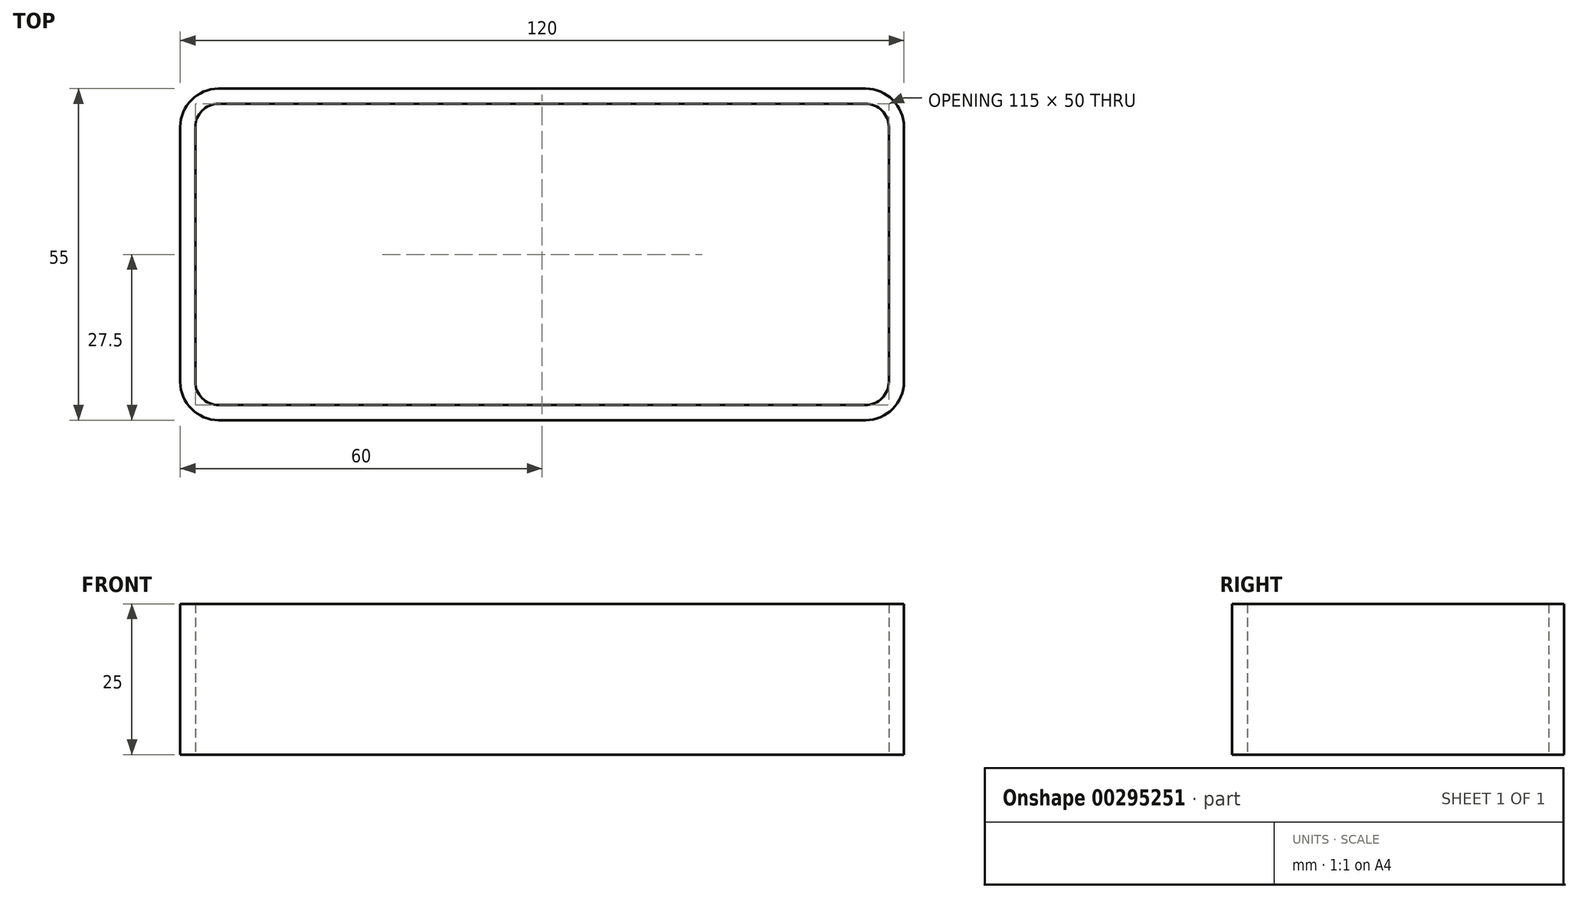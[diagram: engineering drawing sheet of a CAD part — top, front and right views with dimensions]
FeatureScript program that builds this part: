
annotation { "Feature Type Name" : "Feature", "Feature Type Description" : "" }
export const myFeature = defineFeature(function(context is Context, id is Id, definition is map)
    precondition{}
    {
        {
            var Q0;
            Q0=qCreatedBy(makeId("Top.planeOp"),FACE);
            var sketch = newSketch(context, id + "F0", { "sketchPlane" : qUnion([Q0])});
            skLineSegment(sketch, "E0.bottom", {"start": v(53.65, 27.5) * mm, "end": v(-53.65, 27.5) * mm});
            skLineSegment(sketch, "E0.top", {"start": v(53.65, -27.5) * mm, "end": v(-53.65, -27.5) * mm});
            skLineSegment(sketch, "E0.left", {"start": v(60, 21.15) * mm, "end": v(60, -21.15) * mm});
            skLineSegment(sketch, "E0.right", {"start": v(-60, 21.15) * mm, "end": v(-60, -21.15) * mm});
            skPoint(sketch, "E0.middle", {"position": v(0, 0) * mm});
            skPoint(sketch, "E1.visualSharp", {"position": v(-60, 27.5) * mm});
            skArc(sketch, "E1.filletArc", {"start": v(-53.65, 27.5) * mm, "mid": v(-58.14, 25.64) * mm, "end": v(-60, 21.15) * mm});
            skPoint(sketch, "E2.visualSharp", {"position": v(-60, -27.5) * mm});
            skArc(sketch, "E2.filletArc", {"start": v(-60, -21.15) * mm, "mid": v(-58.14, -25.64) * mm, "end": v(-53.65, -27.5) * mm});
            skPoint(sketch, "E3.visualSharp", {"position": v(60, -27.5) * mm});
            skArc(sketch, "E3.filletArc", {"start": v(53.65, -27.5) * mm, "mid": v(58.14, -25.64) * mm, "end": v(60, -21.15) * mm});
            skPoint(sketch, "E4.visualSharp", {"position": v(60, 27.5) * mm});
            skArc(sketch, "E4.filletArc", {"start": v(60, 21.15) * mm, "mid": v(58.14, 25.64) * mm, "end": v(53.65, 27.5) * mm});
            skLineSegment(sketch, "E5.0", {"start": v(53.65, -25) * mm, "end": v(-53.65, -25) * mm});
            skArc(sketch, "E5.1", {"start": v(-57.5, -21.15) * mm, "mid": v(-56.37, -23.87) * mm, "end": v(-53.65, -25) * mm});
            skArc(sketch, "E5.2", {"start": v(53.65, -25) * mm, "mid": v(56.37, -23.87) * mm, "end": v(57.5, -21.15) * mm});
            skLineSegment(sketch, "E5.3", {"start": v(-57.5, 21.15) * mm, "end": v(-57.5, -21.15) * mm});
            skLineSegment(sketch, "E5.4", {"start": v(57.5, 21.15) * mm, "end": v(57.5, -21.15) * mm});
            skArc(sketch, "E5.5", {"start": v(57.5, 21.15) * mm, "mid": v(56.37, 23.87) * mm, "end": v(53.65, 25) * mm});
            skLineSegment(sketch, "E5.6", {"start": v(53.65, 25) * mm, "end": v(-53.65, 25) * mm});
            skArc(sketch, "E5.7", {"start": v(-53.65, 25) * mm, "mid": v(-56.37, 23.87) * mm, "end": v(-57.5, 21.15) * mm});
            skSolve(sketch);
        }
        {
            var Q0;
            Q0 = qSketchRegion(id + "F0", true);
            extrude(context, id + "F1", {"entities" : qUnion([Q0]), "depth" : 25 * mm});
        }
    });
